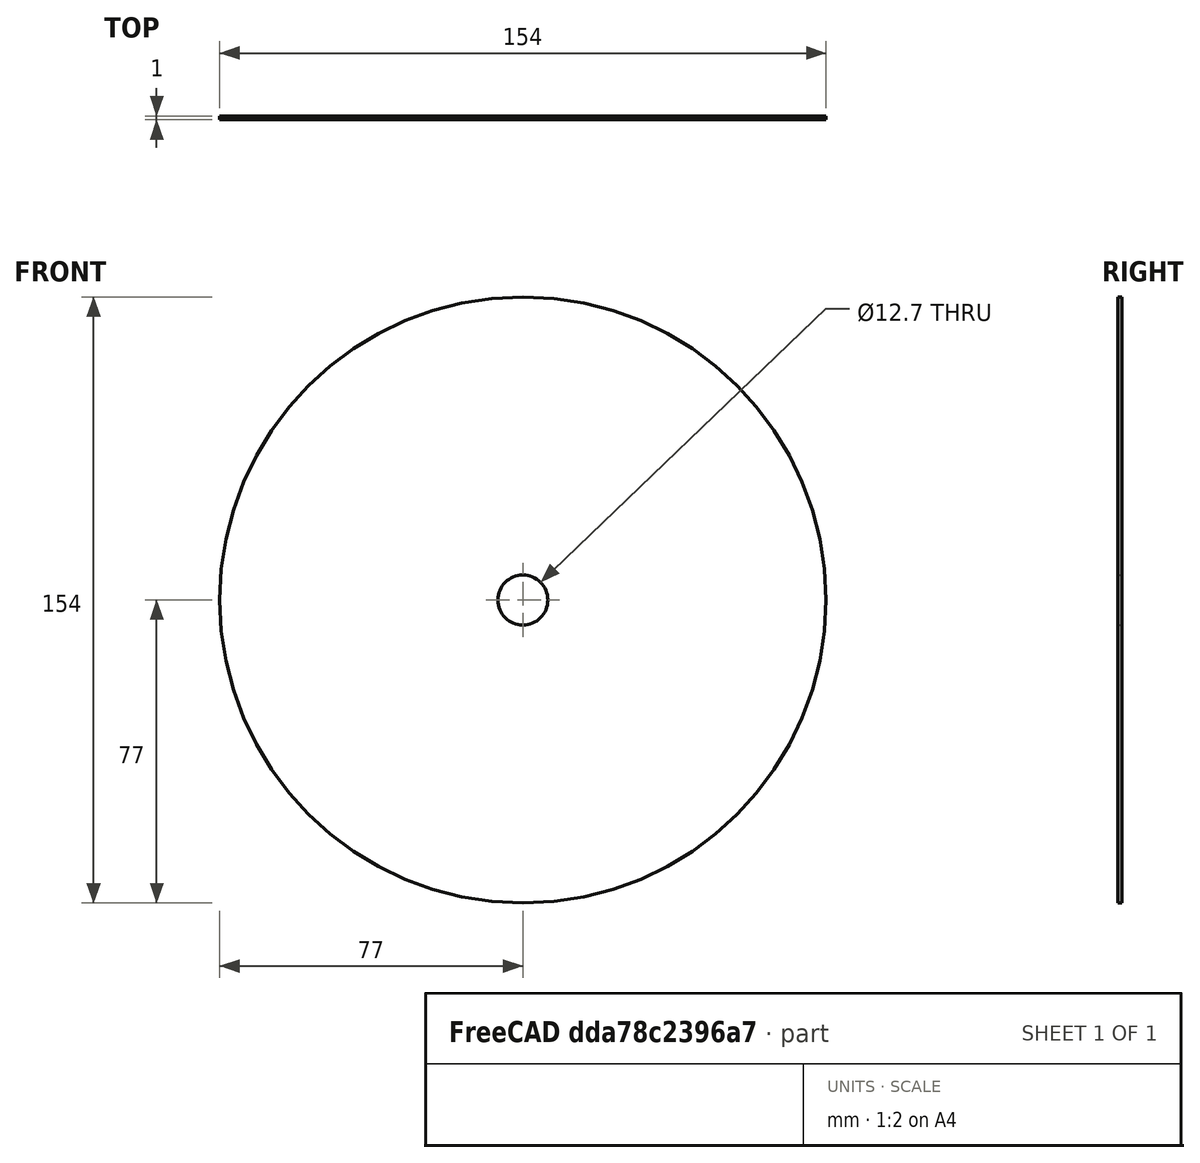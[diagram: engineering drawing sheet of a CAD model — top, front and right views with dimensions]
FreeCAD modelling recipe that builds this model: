
FCSTD DOCUMENT  (FreeCAD 0.19R)
Label: disc
License: All rights reserved
LicenseURL: http://en.wikipedia.org/wiki/All_rights_reserved
objects: TechDraw::DrawViewDimension×4, TechDraw::DrawViewPart×3, PartDesign::CoordinateSystem×2, Sketcher::SketchObject×1, PartDesign::Pad×1, PartDesign::Body×1, TechDraw::DrawSVGTemplate×1, TechDraw::DrawPage×1
note: 6 computed .brp shape members not serialized (recipe doc carries the construction recipe); baked Part::Feature solids carry a one-line shape summary decoded from their .brp

FEATURE [Sketcher::SketchObject] Sketch
  FullyConstrained = true
  MapMode = 5
  Placement = pos=(0,0,0) rot=(1,0,0;1.5708rad)
  Support = -> [XZ_Plane]
  sketch-geometry (2):
    g0: Circle CenterX=0 CenterY=0 CenterZ=0 NormalX=0 NormalY=0 NormalZ=1 AngleXU=0 Radius=77
    g1: Circle CenterX=0 CenterY=0 CenterZ=0 NormalX=0 NormalY=0 NormalZ=1 AngleXU=0 Radius=6.35
  constraints (4):
    c: Coincident(g0,g-1)
    c: Coincident(g1,g0)
    c: Diameter(g1) = 12.7
    c: Diameter(g0) = 154
FEATURE [PartDesign::Pad] Pad
  Direction = (1,1,1)
  Length = 1
  Length2 = 100
  Placement = pos=(0,0,0) rot=(1,0,0;1.5708rad)
  Profile = -> Sketch
  Type = 0
FEATURE [PartDesign::CoordinateSystem] LCS_back
  AttacherType = Attacher::AttachEngine3D
  MapMode = 11
  Placement = pos=(0,0,0) rot=(0.57735,-0.57735,0.57735;2.0944rad)
  Support = -> [Pad]
FEATURE [PartDesign::CoordinateSystem] LCS_disc_front
  AttacherType = Attacher::AttachEngine3D
  MapMode = 11
  Placement = pos=(0,-1,0) rot=(0.57735,-0.57735,0.57735;2.0944rad)
  Support = -> [Pad]
FEATURE [PartDesign::Body] Body
  Group = -> [Sketch,Pad,LCS_back,LCS_disc_front]
  Origin = -> Origin
  Tip = -> Pad
FEATURE [TechDraw::DrawSVGTemplate] Template
  EditableTexts = Designed_by_Name=Designed by Name; Drawing_number=Drawing number; FC-Date=Date; FC-SC=Scale; FC-SH=Sheet; FC-Title=Title; Subtitle=Subtitle; Weight=Weight
  Height = 210
  Orientation = 1
  Width = 297
FEATURE [TechDraw::DrawViewPart] View
  CoarseView = false
  Direction = (0,-1,0)
  Focus = 100
  HardHidden = false
  IsoCount = 0
  IsoHidden = false
  IsoVisible = false
  LockPosition = false
  Perspective = false
  Rotation = 0
  Scale = 0.3
  ScaleType = 0
  SeamHidden = false
  SeamVisible = true
  SmoothHidden = false
  SmoothVisible = true
  Source = -> [Pad]
  X = 80.5
  XDirection = (-0.494,0,-0.83)
  Y = 155
FEATURE [TechDraw::DrawViewPart] View001
  CoarseView = false
  Direction = (0.264,-0.596,0.758)
  Focus = 100
  HardHidden = false
  IsoCount = 0
  IsoHidden = false
  IsoVisible = false
  LockPosition = false
  Perspective = false
  Rotation = 0
  Scale = 0.4
  ScaleType = 0
  SeamHidden = false
  SeamVisible = true
  SmoothHidden = false
  SmoothVisible = true
  Source = -> [Body]
  X = 215.5
  XDirection = (0.492,0.759,0.426)
  Y = 152
FEATURE [TechDraw::DrawViewPart] View002
  CoarseView = false
  Direction = (0,0,1)
  Focus = 100
  HardHidden = false
  IsoCount = 0
  IsoHidden = false
  IsoVisible = false
  LockPosition = false
  Perspective = false
  Rotation = 0
  Scale = 0.7
  ScaleType = 0
  SeamHidden = false
  SeamVisible = true
  SmoothHidden = false
  SmoothVisible = true
  Source = -> [Body]
  X = 90.5
  XDirection = (1,0,0)
  Y = 87
FEATURE [TechDraw::DrawViewDimension] Dimension
  Arbitrary = false
  ArbitraryTolerances = false
  EqualTolerance = true
  FormatSpec = %.2f
  FormatSpecOverTolerance = %+.2f
  FormatSpecUnderTolerance = %+.2f
  Inverted = false
  LockPosition = false
  MeasureType = 1
  OverTolerance = 0
  References2D = -> [View002]
  Rotation = 0
  ScaleType = 0
  TheoreticalExact = false
  Type = 0
  UnderTolerance = 0
  X = 0
  Y = -0.5
FEATURE [TechDraw::DrawViewDimension] Dimension002
  Arbitrary = false
  ArbitraryTolerances = false
  EqualTolerance = true
  FormatSpec = ⌀%.2f
  FormatSpecOverTolerance = %+.2f
  FormatSpecUnderTolerance = %+.2f
  Inverted = false
  LockPosition = false
  MeasureType = 1
  OverTolerance = 0
  References2D = -> [View]
  Rotation = 0
  ScaleType = 0
  TheoreticalExact = false
  Type = 5
  UnderTolerance = 0
  X = -13
  Y = 0
FEATURE [TechDraw::DrawViewDimension] Dimension004
  Arbitrary = false
  ArbitraryTolerances = false
  EqualTolerance = true
  FormatSpec = %.2f
  FormatSpecOverTolerance = %+.2f
  FormatSpecUnderTolerance = %+.2f
  Inverted = false
  LockPosition = false
  MeasureType = 1
  OverTolerance = 0
  References2D = -> [View002]
  Rotation = 0
  ScaleType = 0
  TheoreticalExact = false
  Type = 2
  UnderTolerance = 0
  X = 61.9
  Y = 0
FEATURE [TechDraw::DrawViewDimension] Dimension005
  Arbitrary = false
  ArbitraryTolerances = false
  EqualTolerance = true
  FormatSpec = ⌀%.2f
  FormatSpecOverTolerance = %+.2f
  FormatSpecUnderTolerance = %+.2f
  Inverted = false
  LockPosition = false
  MeasureType = 1
  OverTolerance = 0
  References2D = -> [View]
  Rotation = 0
  ScaleType = 0
  TheoreticalExact = false
  Type = 5
  UnderTolerance = 0
  X = 12
  Y = 0
FEATURE [TechDraw::DrawPage] Page
  KeepUpdated = true
  NextBalloonIndex = 1
  ProjectionType = 0
  Template = -> Template
  Views = -> [View,View001,View002,Dimension,Dimension002,Dimension004,Dimension005]
